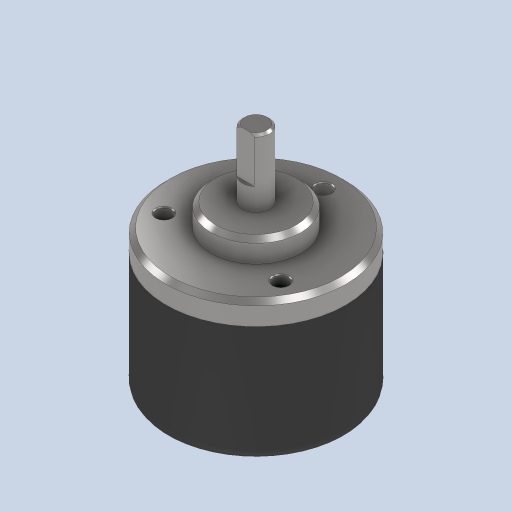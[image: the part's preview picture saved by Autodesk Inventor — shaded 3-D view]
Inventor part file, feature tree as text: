
AUTODESK INVENTOR PART (.ipt)
format: ipt  version: 2023 (Build 270158000, 158)  size: 202,240 bytes
history: native  units: mm
features: sketch x6, extrude x5, chamfer x2, fillet x1, hole x1
ambient origin geometry x8: Origin, YZ Plane, XZ Plane, XY Plane, X Axis, Y Axis, Z Axis, Center Point
bodies: Solid1 (feature_tree)
feature tree (15):
  extrude  "Extrusion1"  Depth=26.0mm TaperAngle=0.0deg
  extrude  "Extrusion2"  Depth=5.0mm TaperAngle=0.0deg
  extrude  "Extrusion3"  Depth=20.0mm TaperAngle=0.0deg
  extrude  "Extrusion4"  Depth=15.0mm TaperAngle=0.0deg
  extrude  "Extrusion5"  Depth=10.0mm TaperAngle=0.0deg
  fillet  "Fillet1"  Radius=2.0mm
  chamfer  "Chamfer1"  Distance=2.0mm Angle=45.0deg
  chamfer  "Chamfer2"  Distance=2.0mm Angle=45.0deg
  hole  "Hole1"  [1 undecoded]
  sketch  "Sketch1"  dims[d0=40.0mm d1=26.0mm d2=0.0mm]
  sketch  "Sketch2"  dims[d3=39.9mm d4=5.0mm d5=0.0mm]
  sketch  "Sketch3"  dims[d6=20.0mm d7=5.0mm d8=0.0mm]
  sketch  "Sketch4"  dims[d9=6.0mm d10=15.0mm d11=0.0mm]
  sketch  "Sketch5"  dims[d12=2.3mm d13=10.0mm d14=0.0mm d15=2.0mm d16=1.0mm d17=2.0mm d18=45.0deg d19=0.5mm d20=2.0mm d21=45.0deg]
  sketch  "Sketch6"  dims[d23=15.0mm d24=30.0mm d26=360.0deg d28=3.4mm d29=6.0mm d30=3.8mm d31=2.0mm d32=90.0deg d33=5.0mm d34=20.594885mm]
note: 1 required parameter value undecoded (feature->parameter linkage not recoverable at this tier; creation-order binding heuristic only, values carry confidence <= 0.55)
